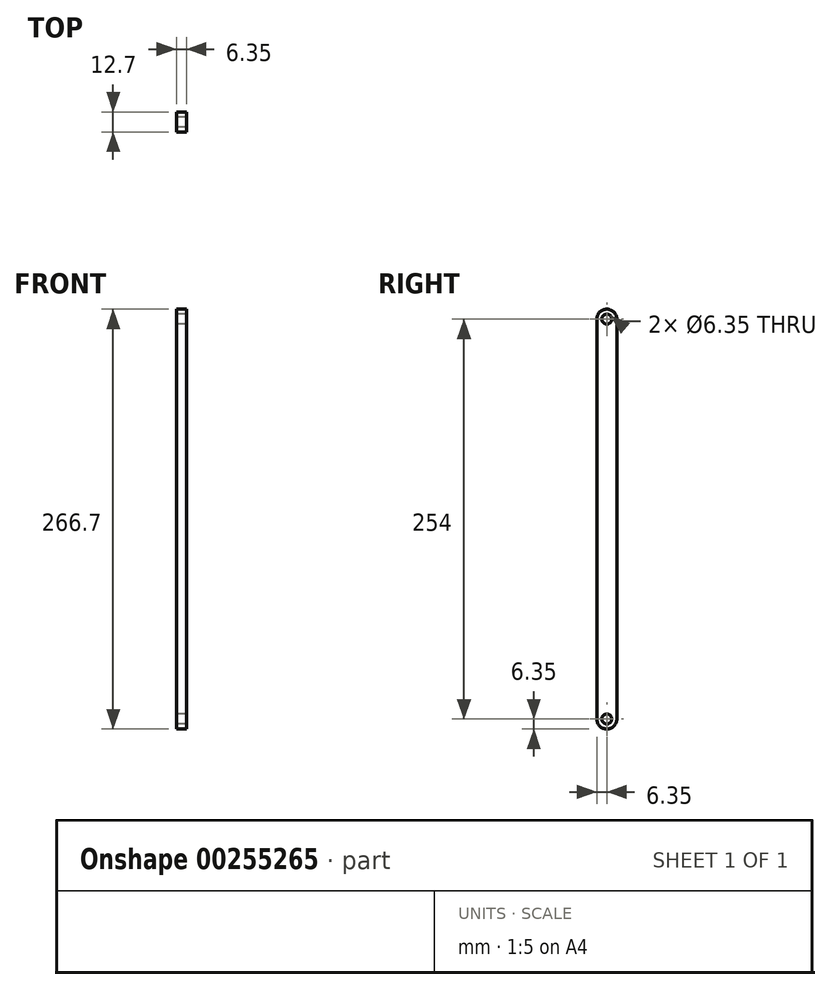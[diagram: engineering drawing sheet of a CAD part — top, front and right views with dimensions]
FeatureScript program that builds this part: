
annotation { "Feature Type Name" : "Feature", "Feature Type Description" : "" }
export const myFeature = defineFeature(function(context is Context, id is Id, definition is map)
    precondition{}
    {
        {
            var Q0;
            Q0=qCreatedBy(makeId("Right.planeOp"),FACE);
            var sketch = newSketch(context, id + "F0", { "sketchPlane" : qUnion([Q0])});
            skCircle(sketch, "E0", {"center": v(0, 0) * mm, "radius": 3.18 * mm});
            skCircle(sketch, "E1", {"center": v(0, 254) * mm, "radius": 3.18 * mm});
            skArc(sketch, "E2", {"start": v(6.35, 254) * mm, "mid": v(0, 260.35) * mm, "end": v(-6.35, 254) * mm});
            skArc(sketch, "E3", {"start": v(-6.35, 0) * mm, "mid": v(0, -6.35) * mm, "end": v(6.35, 0) * mm});
            skLineSegment(sketch, "E4", {"start": v(-6.35, 254) * mm, "end": v(-6.35, 0) * mm});
            skLineSegment(sketch, "E5", {"start": v(6.35, 254) * mm, "end": v(6.35, 0) * mm});
            skSolve(sketch);
        }
        {
            var Q0;
            Q0 = qSketchRegion(id + "F0", true);
            extrude(context, id + "F1", {"entities" : qUnion([Q0]), "depth" : 6.35 * mm});
        }
    });
